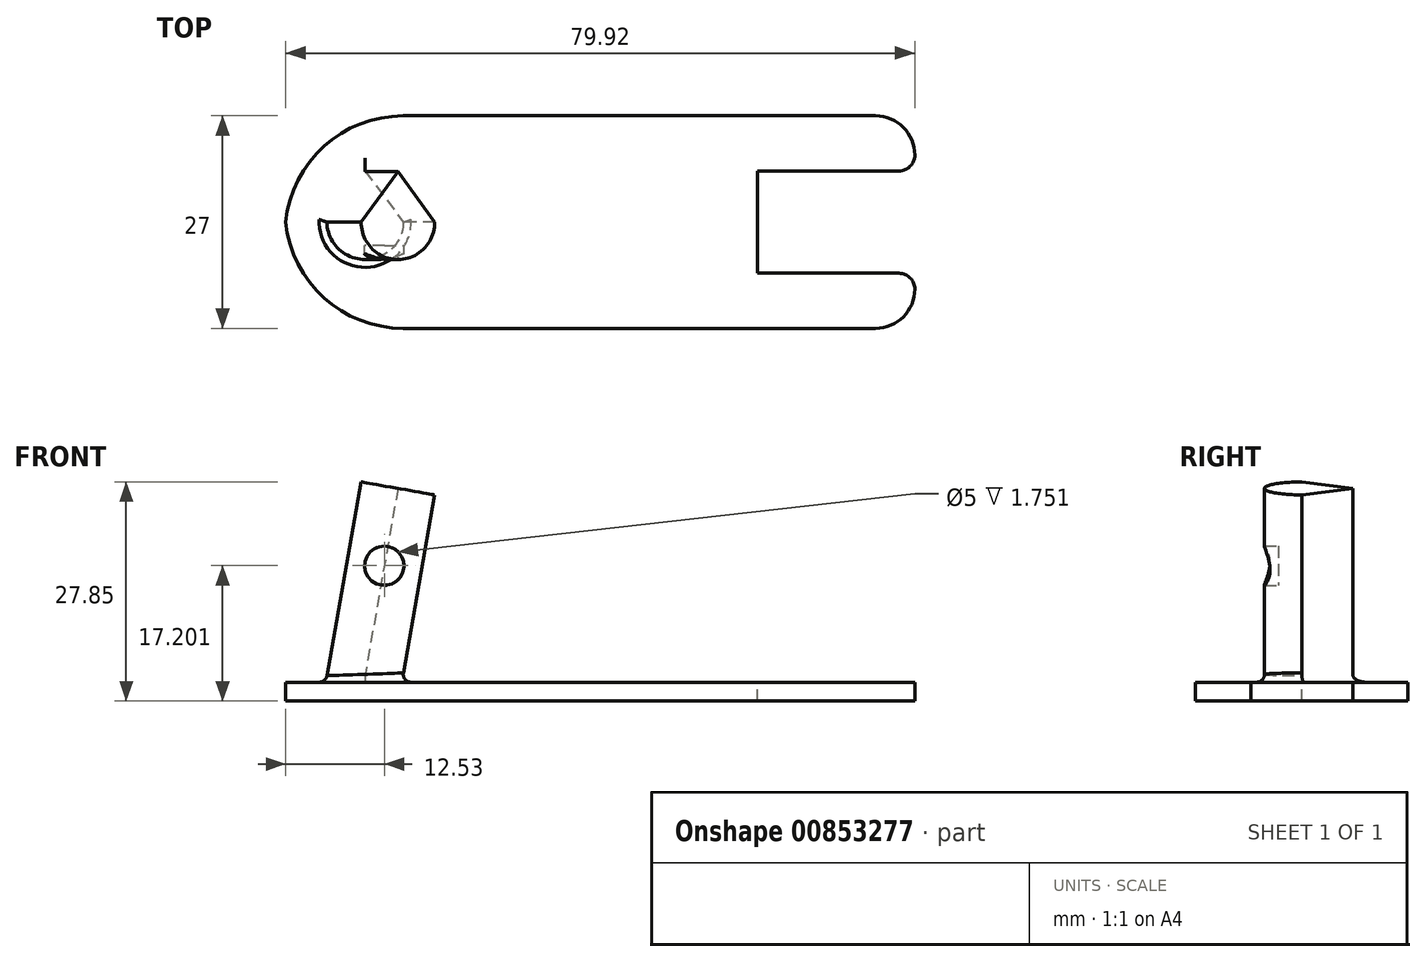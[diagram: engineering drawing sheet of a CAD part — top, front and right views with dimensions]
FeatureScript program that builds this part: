
annotation { "Feature Type Name" : "Feature", "Feature Type Description" : "" }
export const myFeature = defineFeature(function(context is Context, id is Id, definition is map)
    precondition{}
    {
        {
            var Q0;
            Q0=qCreatedBy(makeId("Top.planeOp"),FACE);
            var sketch = newSketch(context, id + "F0", { "sketchPlane" : qUnion([Q0])});
            skLineSegment(sketch, "E0.bottom", {"start": v(-10, 13.5) * mm, "end": v(70, 13.5) * mm});
            skLineSegment(sketch, "E0.top", {"start": v(-10, -13.5) * mm, "end": v(70, -13.5) * mm});
            skLineSegment(sketch, "E0.left", {"start": v(-10, 13.5) * mm, "end": v(-10, -13.5) * mm});
            skLineSegment(sketch, "E0.right", {"start": v(70, 13.5) * mm, "end": v(70, -13.5) * mm});
            skPoint(sketch, "E1", {"position": v(-10, 0) * mm});
            skArc(sketch, "E2", {"start": v(-4.75, 0) * mm, "mid": v(0, -4.75) * mm, "end": v(4.75, 0) * mm});
            skLineSegment(sketch, "E3.bottom", {"start": v(70, 6.5) * mm, "end": v(50, 6.5) * mm});
            skLineSegment(sketch, "E3.top", {"start": v(70, -6.5) * mm, "end": v(50, -6.5) * mm});
            skLineSegment(sketch, "E3.left", {"start": v(70, 6.5) * mm, "end": v(70, -6.5) * mm});
            skLineSegment(sketch, "E3.right", {"start": v(50, 6.5) * mm, "end": v(50, -6.5) * mm});
            skPoint(sketch, "E3.middle", {"position": v(60, 0) * mm});
            skLineSegment(sketch, "E4", {"start": v(4.75, 0) * mm, "end": v(0, 6.45) * mm});
            skLineSegment(sketch, "E5", {"start": v(0, 6.45) * mm, "end": v(-4.75, 0) * mm});
            skPoint(sketch, "E6", {"position": v(0, -4.75) * mm});
            skLineSegment(sketch, "E7", {"start": v(0, 6.45) * mm, "end": v(0, -4.75) * mm, "construction": true});
            skSolve(sketch);
        }
        {
            var Q0;
            {var subQ1=sQuery(id+"F0.wireOp",EDGE,"E0.bottom");Q0=makeQuery(id+"F0.imprint","IMPRINT",FACE,{"disambiguationData":[TD([[makeQuery(id+"F0.imprint","IMPRINT",EDGE,{"derivedFrom":subQ1}),-1.0]])]});}
            var Q1;
            Q1=makeQuery(id+"F0.imprint","IMPRINT",FACE,{"disambiguationData":[TD([[makeQuery(id+"F0.imprint","IMPRINT",EDGE,{"derivedFrom":sQuery(id+"F0.wireOp",EDGE,"E2")}),1.0]])]});
            extrude(context, id + "F1", {"entities" : qUnion([Q0, Q1]), "oppositeDirection" : true, "depth" : 2.4 * mm, "offsetDistance" : 25 * mm});
        }
        {
            var Q0;
            Q0=sQuery(id+"F0.wireOp",EDGE,"E7");
            cPlane(context, id + "F2", {"entities" : qUnion([Q0]), "cplaneType" : CPlaneType.LINE_ANGLE, "offset" : 25 * mm, "angle" : 10 * degree, "oppositeDirection" : true, "width" : 150 * mm, "height" : 150 * mm});
        }
        {
            var Q0;
            Q0=qCreatedBy(id+"F2.planeOp",FACE);
            var sketch = newSketch(context, id + "F3", { "sketchPlane" : qUnion([Q0])});
            skLineSegment(sketch, "E8", {"start": v(-4.75, 0) * mm, "end": v(0, -6.45) * mm});
            skLineSegment(sketch, "E9", {"start": v(0, -6.45) * mm, "end": v(4.75, 0) * mm});
            skArc(sketch, "E10.trimOffspring", {"start": v(4.75, 0) * mm, "mid": v(0, 4.75) * mm, "end": v(-4.75, 0) * mm});
            skSolve(sketch);
        }
        {
            var Q0;
            Q0 = qSketchRegion(id + "F3", true);
            extrude(context, id + "F4", {"entities" : qUnion([Q0]), "operationType" : NewBodyOperationType.ADD, "oppositeDirection" : true, "depth" : 25 * mm, "offsetDistance" : 25 * mm, "hasSecondDirection" : true, "secondDirectionOppositeDirection" : false, "secondDirectionDepth" : 1 * mm});
        }
        {
            var Q0;
            Q0=makeQuery(id+"F1.opExtrude","SWEPT_EDGE",EDGE,{"disambiguationData":[OSD([sQuery(id+"F0.wireOp",EDGE,"E0.top"),sQuery(id+"F0.wireOp",EDGE,"E0.right")])]});
            var Q1;
            Q1=makeQuery(id+"F1.opExtrude","SWEPT_EDGE",EDGE,{"disambiguationData":[OSD([sQuery(id+"F0.wireOp",EDGE,"E0.bottom"),sQuery(id+"F0.wireOp",EDGE,"E0.right")])]});
            fillet(context, id + "F5", {"entities" : qUnion([Q0, Q1]), "radius" : 5 * mm, "tangentPropagation" : true, "allowEdgeOverflow" : false});
        }
        {
            var Q0;
            Q0=makeQuery(id+"F1.opExtrude","SWEPT_EDGE",EDGE,{"disambiguationData":[OSD([sQuery(id+"F0.wireOp",EDGE,"E0.top"),sQuery(id+"F0.wireOp",EDGE,"E0.left")])]});
            var Q1;
            Q1=makeQuery(id+"F1.opExtrude","SWEPT_EDGE",EDGE,{"disambiguationData":[OSD([sQuery(id+"F0.wireOp",EDGE,"E0.bottom"),sQuery(id+"F0.wireOp",EDGE,"E0.left")])]});
            fillet(context, id + "F6", {"entities" : qUnion([Q0, Q1]), "radius" : 15 * mm, "tangentPropagation" : true, "allowEdgeOverflow" : false});
        }
        {
            var Q0;
            Q0=makeQuery(id+"F4.boolean.opBoolean","INTERSECT",EDGE,{"derivedFrom":[makeQuery(id+"F1.opExtrude","CAP_FACE",FACE,{"disambiguationData":[OSD([sQuery(id+"F0.wireOp",EDGE,"E0.bottom"),sQuery(id+"F0.wireOp",EDGE,"E0.top"),sQuery(id+"F0.wireOp",EDGE,"E0.left"),sQuery(id+"F0.wireOp",EDGE,"E0.right"),sQuery(id+"F0.wireOp",EDGE,"E3.bottom"),sQuery(id+"F0.wireOp",EDGE,"E3.top"),sQuery(id+"F0.wireOp",EDGE,"E3.right")])],"isStart":true}),makeQuery(id+"F4.opExtrude","SWEPT_FACE",FACE,{"disambiguationData":[OSD([sQuery(id+"F3.wireOp",EDGE,"E10.trimOffspring")])]})]});
            var Q1;
            Q1=makeQuery(id+"F4.boolean.opBoolean","INTERSECT",EDGE,{"derivedFrom":[makeQuery(id+"F1.opExtrude","CAP_FACE",FACE,{"disambiguationData":[OSD([sQuery(id+"F0.wireOp",EDGE,"E0.bottom"),sQuery(id+"F0.wireOp",EDGE,"E0.top"),sQuery(id+"F0.wireOp",EDGE,"E0.left"),sQuery(id+"F0.wireOp",EDGE,"E0.right"),sQuery(id+"F0.wireOp",EDGE,"E3.bottom"),sQuery(id+"F0.wireOp",EDGE,"E3.top"),sQuery(id+"F0.wireOp",EDGE,"E3.right")])],"isStart":true}),makeQuery(id+"F4.opExtrude","SWEPT_FACE",FACE,{"disambiguationData":[OSD([sQuery(id+"F3.wireOp",EDGE,"E8")])]})]});
            var Q2;
            Q2=makeQuery(id+"F4.boolean.opBoolean","INTERSECT",EDGE,{"derivedFrom":[makeQuery(id+"F1.opExtrude","CAP_FACE",FACE,{"disambiguationData":[OSD([sQuery(id+"F0.wireOp",EDGE,"E0.bottom"),sQuery(id+"F0.wireOp",EDGE,"E0.top"),sQuery(id+"F0.wireOp",EDGE,"E0.left"),sQuery(id+"F0.wireOp",EDGE,"E0.right"),sQuery(id+"F0.wireOp",EDGE,"E3.bottom"),sQuery(id+"F0.wireOp",EDGE,"E3.top"),sQuery(id+"F0.wireOp",EDGE,"E3.right")])],"isStart":true}),makeQuery(id+"F4.opExtrude","SWEPT_FACE",FACE,{"disambiguationData":[OSD([sQuery(id+"F3.wireOp",EDGE,"E9")])]})]});
            fillet(context, id + "F7", {"entities" : qUnion([Q0, Q1, Q2]), "radius" : 1 * mm, "tangentPropagation" : true, "allowEdgeOverflow" : false});
        }
        {
            var Q0;
            Q0=makeQuery(id+"F1.opExtrude","SWEPT_EDGE",EDGE,{"disambiguationData":[OSD([sQuery(id+"F0.wireOp",EDGE,"E0.right"),sQuery(id+"F0.wireOp",EDGE,"E3.bottom"),sQuery(id+"F0.wireOp",EDGE,"E3.left")])]});
            var Q1;
            Q1=makeQuery(id+"F1.opExtrude","SWEPT_EDGE",EDGE,{"disambiguationData":[OSD([sQuery(id+"F0.wireOp",EDGE,"E0.right"),sQuery(id+"F0.wireOp",EDGE,"E3.top"),sQuery(id+"F0.wireOp",EDGE,"E3.left")])]});
            fillet(context, id + "F8", {"entities" : qUnion([Q0, Q1]), "radius" : 2 * mm, "tangentPropagation" : true, "allowEdgeOverflow" : false});
        }
        {
            var Q0;
            Q0=qCreatedBy(makeId("Front.planeOp"),FACE);
            var sketch = newSketch(context, id + "F9", { "sketchPlane" : qUnion([Q0])});
            skCircle(sketch, "E11", {"center": v(2.6, 14.8) * mm, "radius": 2.5 * mm});
            skLineSegment(sketch, "E12.0", {"start": v(4.34, 24.62) * mm, "end": v(0.2, 1.14) * mm});
            skSolve(sketch);
        }
        {
            var Q0;
            Q0 = qSketchRegion(id + "F9", true);
            extrude(context, id + "F10", {"entities" : qUnion([Q0]), "operationType" : NewBodyOperationType.REMOVE, "depth" : 25 * mm, "offsetDistance" : 25 * mm, "hasSecondDirection" : true, "secondDirectionOppositeDirection" : false, "secondDirectionDepth" : 3 * mm});
        }
    });
